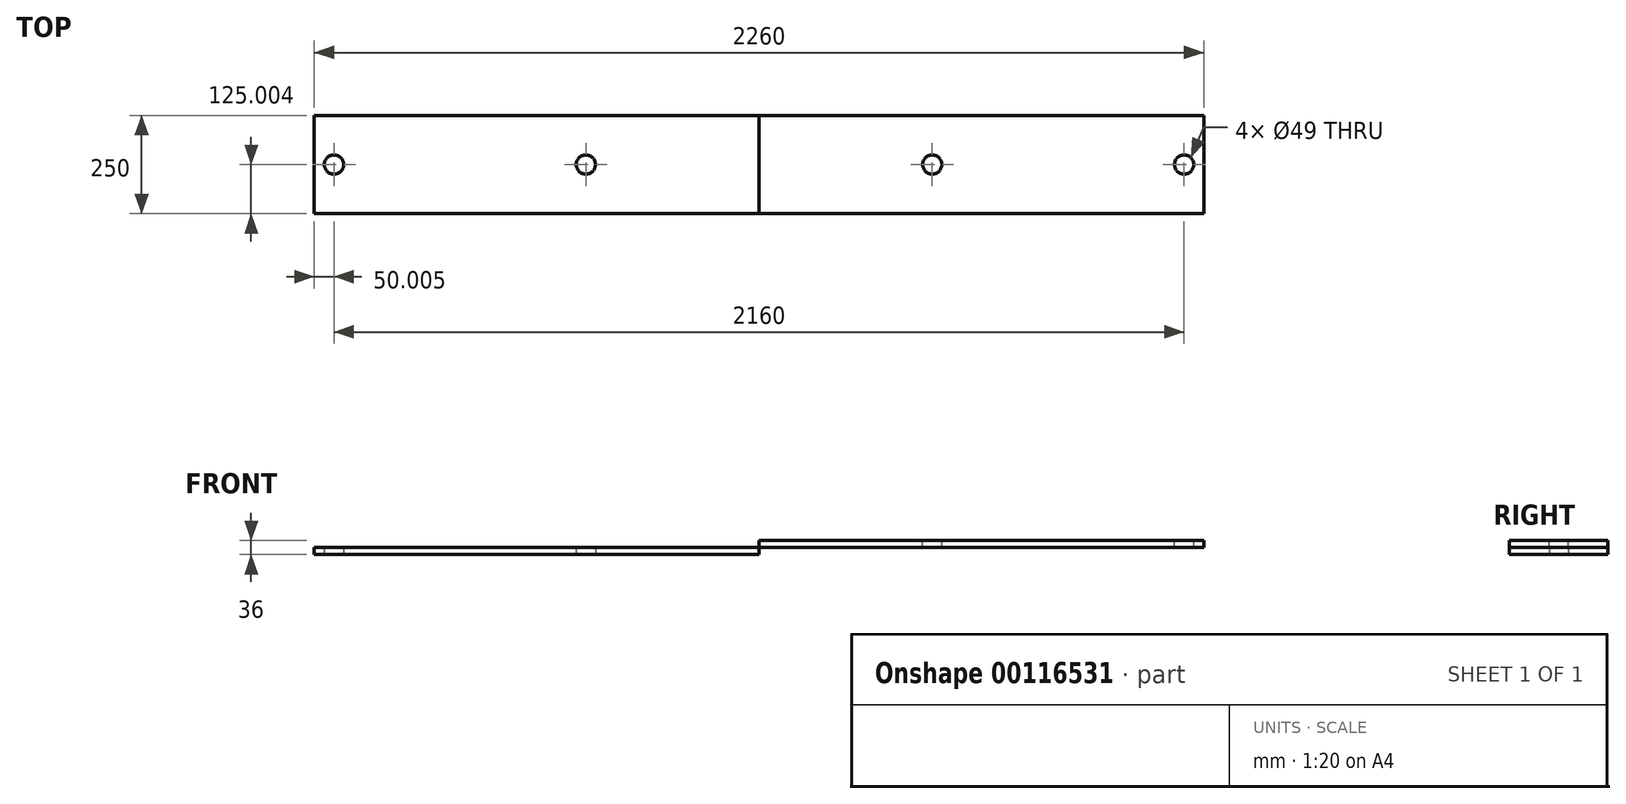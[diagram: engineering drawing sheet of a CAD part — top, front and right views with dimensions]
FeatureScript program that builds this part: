
annotation { "Feature Type Name" : "Feature", "Feature Type Description" : "" }
export const myFeature = defineFeature(function(context is Context, id is Id, definition is map)
    precondition{}
    {
        {
            var Q0;
            Q0=qCreatedBy(makeId("Top.planeOp"),FACE);
            var sketch = newSketch(context, id + "F0", { "sketchPlane" : qUnion([Q0])});
            skLineSegment(sketch, "E0.bottom", {"start": v(142.52, 285.12) * mm, "end": v(1272.52, 285.12) * mm});
            skLineSegment(sketch, "E0.top", {"start": v(142.52, 35.12) * mm, "end": v(1272.52, 35.12) * mm});
            skLineSegment(sketch, "E0.left", {"start": v(142.52, 285.12) * mm, "end": v(142.52, 35.12) * mm});
            skLineSegment(sketch, "E0.right", {"start": v(1272.52, 285.12) * mm, "end": v(1272.52, 35.12) * mm});
            skLineSegment(sketch, "E1", {"start": v(142.52, 160.12) * mm, "end": v(1272.52, 160.12) * mm, "construction": true});
            skCircle(sketch, "E2", {"center": v(192.52, 160.12) * mm, "radius": 24.5 * mm});
            skCircle(sketch, "E3", {"center": v(832.52, 160.12) * mm, "radius": 24.5 * mm});
            skSolve(sketch);
        }
        {
            var Q0;
            Q0=makeQuery(id+"F0.imprint","IMPRINT",FACE,{"disambiguationData":[TD([[makeQuery(id+"F0.imprint","IMPRINT",EDGE,{"derivedFrom":sQuery(id+"F0.wireOp",EDGE,"E0.bottom")}),-1.0]])]});
            var Q1;
            Q1=makeQuery(id+"F0.imprint","IMPRINT",FACE,{"disambiguationData":[TD([[makeQuery(id+"F0.imprint","IMPRINT",EDGE,{"derivedFrom":sQuery(id+"F0.wireOp",EDGE,"E0.bottom")}),-1.0]])]});
            var Q2;
            {var subQ0=sQuery(id+"F0.wireOp",EDGE,"E0.left");Q2=makeQuery(id+"F0.imprint","IMPRINT",FACE,{"disambiguationData":[TD([[makeQuery(id+"F0.imprint","IMPRINT",EDGE,{"derivedFrom":subQ0}),1.0]])]});}
            extrude(context, id + "F1", {"entities" : qUnion([Q0, Q1, Q2]), "depth" : 18 * mm});
        }
        {
            var Q0;
            Q0=makeQuery(id+"F1.opExtrude","SWEPT_BODY",BODY,{"disambiguationData":[OSD([sQuery(id+"F0.wireOp",EDGE,"E0.bottom"),sQuery(id+"F0.wireOp",EDGE,"E0.top"),sQuery(id+"F0.wireOp",EDGE,"E0.left"),sQuery(id+"F0.wireOp",EDGE,"E0.right"),sQuery(id+"F0.wireOp",EDGE,"E2"),sQuery(id+"F0.wireOp",EDGE,"E3")])]});
            var Q1;
            Q1=makeQuery(id+"F1.opExtrude","CAP_EDGE",EDGE,{"disambiguationData":[OSD([sQuery(id+"F0.wireOp",EDGE,"E0.right")])],"isStart":false});
            transform(context, id + "F2", {"entities" : qUnion([Q0]), "transformType" : TransformType.ROTATION, "transformAxis" : qUnion([Q1]), "angle" : 180 * degree, "makeCopy" : true});
        }
    });
